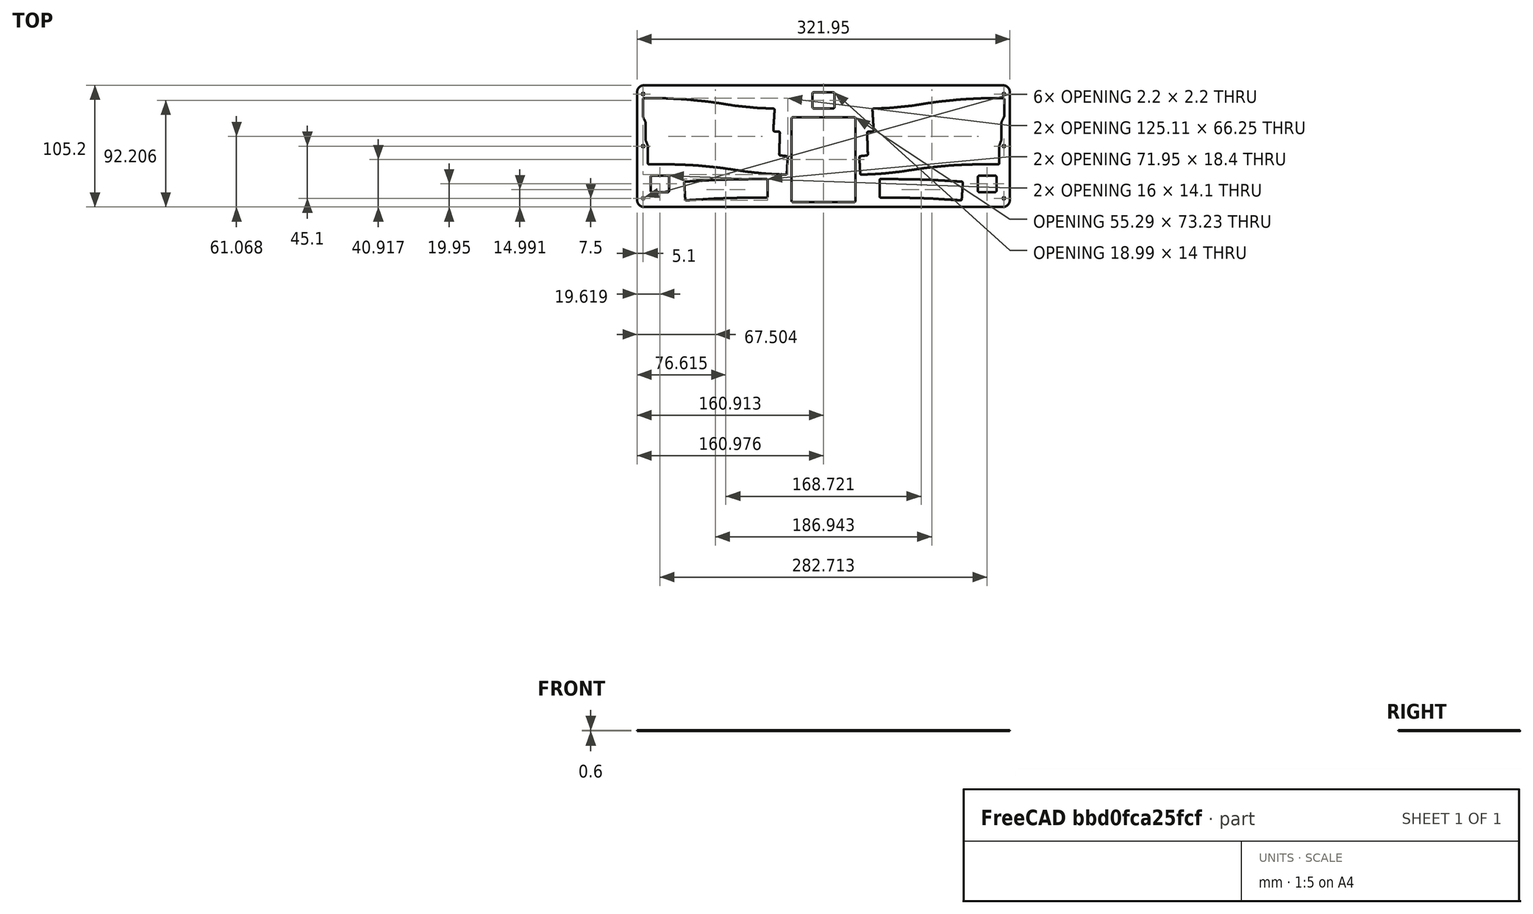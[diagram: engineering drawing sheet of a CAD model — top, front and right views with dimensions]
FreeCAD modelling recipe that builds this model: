
FCSTD DOCUMENT  (FreeCAD 1.0R39109 (Git))
Label: Woorden_decorate
License: All rights reserved
LicenseURL: http://en.wikipedia.org/wiki/All_rights_reserved
objects: Sketcher::SketchObject×1, PartDesign::Pad×1, PartDesign::Body×1
note: 6 computed .brp shape members not serialized (recipe doc carries the construction recipe); baked Part::Feature solids carry a one-line shape summary decoded from their .brp

FEATURE [Sketcher::SketchObject] Sketch
  ArcFitTolerance = 1e-06
  FullyConstrained = false
  MakeInternals = false
  sketch-geometry (177):
    g0: BSplineCurve PolesCount=2 KnotsCount=2 Degree=1 IsPeriodic=0
    g1: BSplineCurve PolesCount=3 KnotsCount=2 Degree=2 IsPeriodic=0
    g2: BSplineCurve PolesCount=3 KnotsCount=2 Degree=2 IsPeriodic=0
    g3: BSplineCurve PolesCount=3 KnotsCount=2 Degree=2 IsPeriodic=0
    g4: BSplineCurve PolesCount=3 KnotsCount=2 Degree=2 IsPeriodic=0
    g5: BSplineCurve PolesCount=3 KnotsCount=2 Degree=2 IsPeriodic=0
    g6: BSplineCurve PolesCount=3 KnotsCount=2 Degree=2 IsPeriodic=0
    g7: BSplineCurve PolesCount=3 KnotsCount=2 Degree=2 IsPeriodic=0
    g8: BSplineCurve PolesCount=3 KnotsCount=2 Degree=2 IsPeriodic=0
    g9: BSplineCurve PolesCount=2 KnotsCount=2 Degree=1 IsPeriodic=0
    g10: BSplineCurve PolesCount=2 KnotsCount=2 Degree=1 IsPeriodic=0
    g11: BSplineCurve PolesCount=2 KnotsCount=2 Degree=1 IsPeriodic=0
    g12: BSplineCurve PolesCount=2 KnotsCount=2 Degree=1 IsPeriodic=0
    g13: BSplineCurve PolesCount=2 KnotsCount=2 Degree=1 IsPeriodic=0
    g14: BSplineCurve PolesCount=2 KnotsCount=2 Degree=1 IsPeriodic=0
    g15: BSplineCurve PolesCount=2 KnotsCount=2 Degree=1 IsPeriodic=0
    g16: BSplineCurve PolesCount=2 KnotsCount=2 Degree=1 IsPeriodic=0
    g17: BSplineCurve PolesCount=3 KnotsCount=2 Degree=2 IsPeriodic=0
    g18: BSplineCurve PolesCount=2 KnotsCount=2 Degree=1 IsPeriodic=0
    g19: BSplineCurve PolesCount=3 KnotsCount=2 Degree=2 IsPeriodic=0
    g20: BSplineCurve PolesCount=3 KnotsCount=2 Degree=2 IsPeriodic=0
    g21: BSplineCurve PolesCount=2 KnotsCount=2 Degree=1 IsPeriodic=0
    g22: BSplineCurve PolesCount=3 KnotsCount=2 Degree=2 IsPeriodic=0
    g23: BSplineCurve PolesCount=2 KnotsCount=2 Degree=1 IsPeriodic=0
    g24: BSplineCurve PolesCount=3 KnotsCount=2 Degree=2 IsPeriodic=0
    g25: BSplineCurve PolesCount=2 KnotsCount=2 Degree=1 IsPeriodic=0
    g26: BSplineCurve PolesCount=2 KnotsCount=2 Degree=1 IsPeriodic=0
    g27: BSplineCurve PolesCount=2 KnotsCount=2 Degree=1 IsPeriodic=0
    g28: BSplineCurve PolesCount=2 KnotsCount=2 Degree=1 IsPeriodic=0
    g29: BSplineCurve PolesCount=3 KnotsCount=2 Degree=2 IsPeriodic=0
    g30: BSplineCurve PolesCount=3 KnotsCount=2 Degree=2 IsPeriodic=0
    g31: BSplineCurve PolesCount=2 KnotsCount=2 Degree=1 IsPeriodic=0
    g32: BSplineCurve PolesCount=2 KnotsCount=2 Degree=1 IsPeriodic=0
    g33: BSplineCurve PolesCount=2 KnotsCount=2 Degree=1 IsPeriodic=0
    g34: BSplineCurve PolesCount=2 KnotsCount=2 Degree=1 IsPeriodic=0
    g35: BSplineCurve PolesCount=3 KnotsCount=2 Degree=2 IsPeriodic=0
    g36: BSplineCurve PolesCount=2 KnotsCount=2 Degree=1 IsPeriodic=0
    g37: BSplineCurve PolesCount=2 KnotsCount=2 Degree=1 IsPeriodic=0
    g38: BSplineCurve PolesCount=3 KnotsCount=2 Degree=2 IsPeriodic=0
    g39: BSplineCurve PolesCount=2 KnotsCount=2 Degree=1 IsPeriodic=0
    g40: BSplineCurve PolesCount=3 KnotsCount=2 Degree=2 IsPeriodic=0
    g41: BSplineCurve PolesCount=2 KnotsCount=2 Degree=1 IsPeriodic=0
    g42: BSplineCurve PolesCount=3 KnotsCount=2 Degree=2 IsPeriodic=0
    g43: BSplineCurve PolesCount=2 KnotsCount=2 Degree=1 IsPeriodic=0
    g44: BSplineCurve PolesCount=2 KnotsCount=2 Degree=1 IsPeriodic=0
    g45: BSplineCurve PolesCount=2 KnotsCount=2 Degree=1 IsPeriodic=0
    g46: BSplineCurve PolesCount=2 KnotsCount=2 Degree=1 IsPeriodic=0
    g47: BSplineCurve PolesCount=2 KnotsCount=2 Degree=1 IsPeriodic=0
    g48: BSplineCurve PolesCount=3 KnotsCount=2 Degree=2 IsPeriodic=0
    g49: BSplineCurve PolesCount=2 KnotsCount=2 Degree=1 IsPeriodic=0
    g50: BSplineCurve PolesCount=3 KnotsCount=2 Degree=2 IsPeriodic=0
    g51: BSplineCurve PolesCount=2 KnotsCount=2 Degree=1 IsPeriodic=0
    g52: BSplineCurve PolesCount=2 KnotsCount=2 Degree=1 IsPeriodic=0
    g53: BSplineCurve PolesCount=2 KnotsCount=2 Degree=1 IsPeriodic=0
    g54: BSplineCurve PolesCount=3 KnotsCount=2 Degree=2 IsPeriodic=0
    g55: BSplineCurve PolesCount=3 KnotsCount=2 Degree=2 IsPeriodic=0
    g56: BSplineCurve PolesCount=2 KnotsCount=2 Degree=1 IsPeriodic=0
    g57: BSplineCurve PolesCount=2 KnotsCount=2 Degree=1 IsPeriodic=0
    g58: BSplineCurve PolesCount=2 KnotsCount=2 Degree=1 IsPeriodic=0
    g59: BSplineCurve PolesCount=2 KnotsCount=2 Degree=1 IsPeriodic=0
    g60: BSplineCurve PolesCount=2 KnotsCount=2 Degree=1 IsPeriodic=0
    g61: BSplineCurve PolesCount=2 KnotsCount=2 Degree=1 IsPeriodic=0
    g62: BSplineCurve PolesCount=2 KnotsCount=2 Degree=1 IsPeriodic=0
    g63: BSplineCurve PolesCount=2 KnotsCount=2 Degree=1 IsPeriodic=0
    g64: BSplineCurve PolesCount=2 KnotsCount=2 Degree=1 IsPeriodic=0
    g65: BSplineCurve PolesCount=2 KnotsCount=2 Degree=1 IsPeriodic=0
    g66: BSplineCurve PolesCount=2 KnotsCount=2 Degree=1 IsPeriodic=0
    g67: BSplineCurve PolesCount=3 KnotsCount=2 Degree=2 IsPeriodic=0
    g68: BSplineCurve PolesCount=2 KnotsCount=2 Degree=1 IsPeriodic=0
    g69: BSplineCurve PolesCount=2 KnotsCount=2 Degree=1 IsPeriodic=0
    g70: BSplineCurve PolesCount=3 KnotsCount=2 Degree=2 IsPeriodic=0
    g71: BSplineCurve PolesCount=3 KnotsCount=2 Degree=2 IsPeriodic=0
    g72: BSplineCurve PolesCount=3 KnotsCount=2 Degree=2 IsPeriodic=0
    g73: BSplineCurve PolesCount=2 KnotsCount=2 Degree=1 IsPeriodic=0
    g74: BSplineCurve PolesCount=3 KnotsCount=2 Degree=2 IsPeriodic=0
    g75: BSplineCurve PolesCount=2 KnotsCount=2 Degree=1 IsPeriodic=0
    g76: BSplineCurve PolesCount=3 KnotsCount=2 Degree=2 IsPeriodic=0
    g77: BSplineCurve PolesCount=2 KnotsCount=2 Degree=1 IsPeriodic=0
    g78: BSplineCurve PolesCount=3 KnotsCount=2 Degree=2 IsPeriodic=0
    g79: BSplineCurve PolesCount=3 KnotsCount=2 Degree=2 IsPeriodic=0
    g80: BSplineCurve PolesCount=3 KnotsCount=2 Degree=2 IsPeriodic=0
    g81: BSplineCurve PolesCount=3 KnotsCount=2 Degree=2 IsPeriodic=0
    g82: BSplineCurve PolesCount=2 KnotsCount=2 Degree=1 IsPeriodic=0
    g83: BSplineCurve PolesCount=3 KnotsCount=2 Degree=2 IsPeriodic=0
    g84: BSplineCurve PolesCount=2 KnotsCount=2 Degree=1 IsPeriodic=0
    g85: BSplineCurve PolesCount=2 KnotsCount=2 Degree=1 IsPeriodic=0
    g86: BSplineCurve PolesCount=2 KnotsCount=2 Degree=1 IsPeriodic=0
    g87: BSplineCurve PolesCount=3 KnotsCount=2 Degree=2 IsPeriodic=0
    g88: BSplineCurve PolesCount=2 KnotsCount=2 Degree=1 IsPeriodic=0
    g89: BSplineCurve PolesCount=3 KnotsCount=2 Degree=2 IsPeriodic=0
    g90: BSplineCurve PolesCount=2 KnotsCount=2 Degree=1 IsPeriodic=0
    g91: BSplineCurve PolesCount=2 KnotsCount=2 Degree=1 IsPeriodic=0
    g92: BSplineCurve PolesCount=2 KnotsCount=2 Degree=1 IsPeriodic=0
    g93: BSplineCurve PolesCount=3 KnotsCount=2 Degree=2 IsPeriodic=0
    g94: BSplineCurve PolesCount=3 KnotsCount=2 Degree=2 IsPeriodic=0
    g95: BSplineCurve PolesCount=2 KnotsCount=2 Degree=1 IsPeriodic=0
    g96: BSplineCurve PolesCount=2 KnotsCount=2 Degree=1 IsPeriodic=0
    g97: BSplineCurve PolesCount=2 KnotsCount=2 Degree=1 IsPeriodic=0
    g98: BSplineCurve PolesCount=2 KnotsCount=2 Degree=1 IsPeriodic=0
    g99: BSplineCurve PolesCount=2 KnotsCount=2 Degree=1 IsPeriodic=0
    g100: BSplineCurve PolesCount=3 KnotsCount=2 Degree=2 IsPeriodic=0
    g101: BSplineCurve PolesCount=3 KnotsCount=2 Degree=2 IsPeriodic=0
    g102: BSplineCurve PolesCount=2 KnotsCount=2 Degree=1 IsPeriodic=0
    g103: BSplineCurve PolesCount=3 KnotsCount=2 Degree=2 IsPeriodic=0
    g104: BSplineCurve PolesCount=2 KnotsCount=2 Degree=1 IsPeriodic=0
    g105: BSplineCurve PolesCount=3 KnotsCount=2 Degree=2 IsPeriodic=0
    g106: BSplineCurve PolesCount=2 KnotsCount=2 Degree=1 IsPeriodic=0
    g107: BSplineCurve PolesCount=3 KnotsCount=2 Degree=2 IsPeriodic=0
    g108: BSplineCurve PolesCount=3 KnotsCount=2 Degree=2 IsPeriodic=0
    g109: BSplineCurve PolesCount=2 KnotsCount=2 Degree=1 IsPeriodic=0
    g110: BSplineCurve PolesCount=2 KnotsCount=2 Degree=1 IsPeriodic=0
    g111: BSplineCurve PolesCount=2 KnotsCount=2 Degree=1 IsPeriodic=0
    g112: BSplineCurve PolesCount=3 KnotsCount=2 Degree=2 IsPeriodic=0
    g113: BSplineCurve PolesCount=2 KnotsCount=2 Degree=1 IsPeriodic=0
    g114: BSplineCurve PolesCount=2 KnotsCount=2 Degree=1 IsPeriodic=0
    g115: BSplineCurve PolesCount=2 KnotsCount=2 Degree=1 IsPeriodic=0
    g116: BSplineCurve PolesCount=2 KnotsCount=2 Degree=1 IsPeriodic=0
    g117: BSplineCurve PolesCount=2 KnotsCount=2 Degree=1 IsPeriodic=0
    g118: BSplineCurve PolesCount=2 KnotsCount=2 Degree=1 IsPeriodic=0
    g119: BSplineCurve PolesCount=3 KnotsCount=2 Degree=2 IsPeriodic=0
    g120: BSplineCurve PolesCount=2 KnotsCount=2 Degree=1 IsPeriodic=0
    g121: BSplineCurve PolesCount=3 KnotsCount=2 Degree=2 IsPeriodic=0
    g122: BSplineCurve PolesCount=2 KnotsCount=2 Degree=1 IsPeriodic=0
    g123: BSplineCurve PolesCount=3 KnotsCount=2 Degree=2 IsPeriodic=0
    g124: BSplineCurve PolesCount=2 KnotsCount=2 Degree=1 IsPeriodic=0
    g125: BSplineCurve PolesCount=2 KnotsCount=2 Degree=1 IsPeriodic=0
    g126: BSplineCurve PolesCount=2 KnotsCount=2 Degree=1 IsPeriodic=0
    g127: BSplineCurve PolesCount=2 KnotsCount=2 Degree=1 IsPeriodic=0
    g128: BSplineCurve PolesCount=3 KnotsCount=2 Degree=2 IsPeriodic=0
    g129: BSplineCurve PolesCount=2 KnotsCount=2 Degree=1 IsPeriodic=0
    g130: BSplineCurve PolesCount=3 KnotsCount=2 Degree=2 IsPeriodic=0
    g131: BSplineCurve PolesCount=3 KnotsCount=2 Degree=2 IsPeriodic=0
    g132: BSplineCurve PolesCount=2 KnotsCount=2 Degree=1 IsPeriodic=0
    g133: BSplineCurve PolesCount=3 KnotsCount=2 Degree=2 IsPeriodic=0
    g134: BSplineCurve PolesCount=3 KnotsCount=2 Degree=2 IsPeriodic=0
    g135: BSplineCurve PolesCount=3 KnotsCount=2 Degree=2 IsPeriodic=0
    g136: BSplineCurve PolesCount=3 KnotsCount=2 Degree=2 IsPeriodic=0
    g137: BSplineCurve PolesCount=2 KnotsCount=2 Degree=1 IsPeriodic=0
    g138: BSplineCurve PolesCount=2 KnotsCount=2 Degree=1 IsPeriodic=0
    g139: BSplineCurve PolesCount=2 KnotsCount=2 Degree=1 IsPeriodic=0
    g140: BSplineCurve PolesCount=2 KnotsCount=2 Degree=1 IsPeriodic=0
    g141: BSplineCurve PolesCount=2 KnotsCount=2 Degree=1 IsPeriodic=0
    g142: BSplineCurve PolesCount=2 KnotsCount=2 Degree=1 IsPeriodic=0
    g143: BSplineCurve PolesCount=3 KnotsCount=2 Degree=2 IsPeriodic=0
    g144: BSplineCurve PolesCount=3 KnotsCount=2 Degree=2 IsPeriodic=0
    g145: BSplineCurve PolesCount=3 KnotsCount=2 Degree=2 IsPeriodic=0
    g146: BSplineCurve PolesCount=2 KnotsCount=2 Degree=1 IsPeriodic=0
    g147: BSplineCurve PolesCount=3 KnotsCount=2 Degree=2 IsPeriodic=0
    g148: BSplineCurve PolesCount=2 KnotsCount=2 Degree=1 IsPeriodic=0
    g149: BSplineCurve PolesCount=3 KnotsCount=2 Degree=2 IsPeriodic=0
    g150: BSplineCurve PolesCount=2 KnotsCount=2 Degree=1 IsPeriodic=0
    g151: BSplineCurve PolesCount=3 KnotsCount=2 Degree=2 IsPeriodic=0
    g152: BSplineCurve PolesCount=2 KnotsCount=2 Degree=1 IsPeriodic=0
    g153: BSplineCurve PolesCount=2 KnotsCount=2 Degree=1 IsPeriodic=0
    g154: BSplineCurve PolesCount=2 KnotsCount=2 Degree=1 IsPeriodic=0
    g155: BSplineCurve PolesCount=3 KnotsCount=2 Degree=2 IsPeriodic=0
    g156: BSplineCurve PolesCount=2 KnotsCount=2 Degree=1 IsPeriodic=0
    g157: BSplineCurve PolesCount=2 KnotsCount=2 Degree=1 IsPeriodic=0
    g158: BSplineCurve PolesCount=2 KnotsCount=2 Degree=1 IsPeriodic=0
    g159: BSplineCurve PolesCount=2 KnotsCount=2 Degree=1 IsPeriodic=0
    g160: BSplineCurve PolesCount=3 KnotsCount=2 Degree=2 IsPeriodic=0
    g161: BSplineCurve PolesCount=3 KnotsCount=2 Degree=2 IsPeriodic=0
    g162: BSplineCurve PolesCount=2 KnotsCount=2 Degree=1 IsPeriodic=0
    g163: BSplineCurve PolesCount=2 KnotsCount=2 Degree=1 IsPeriodic=0
    g164: BSplineCurve PolesCount=2 KnotsCount=2 Degree=1 IsPeriodic=0
    g165: BSplineCurve PolesCount=3 KnotsCount=2 Degree=2 IsPeriodic=0
    g166: BSplineCurve PolesCount=2 KnotsCount=2 Degree=1 IsPeriodic=0
    g167: BSplineCurve PolesCount=2 KnotsCount=2 Degree=1 IsPeriodic=0
    g168: BSplineCurve PolesCount=2 KnotsCount=2 Degree=1 IsPeriodic=0
    g169: BSplineCurve PolesCount=2 KnotsCount=2 Degree=1 IsPeriodic=0
    g170: BSplineCurve PolesCount=2 KnotsCount=2 Degree=1 IsPeriodic=0
    g171: BSplineCurve PolesCount=7 KnotsCount=4 Degree=2 IsPeriodic=0
    g172: BSplineCurve PolesCount=7 KnotsCount=4 Degree=2 IsPeriodic=0
    g173: BSplineCurve PolesCount=7 KnotsCount=4 Degree=2 IsPeriodic=0
    g174: BSplineCurve PolesCount=7 KnotsCount=4 Degree=2 IsPeriodic=0
    g175: BSplineCurve PolesCount=7 KnotsCount=4 Degree=2 IsPeriodic=0
    g176: BSplineCurve PolesCount=7 KnotsCount=4 Degree=2 IsPeriodic=0
  constraints (13):
    c: Coincident(g160,g97)
    c: Coincident(g112,g92)
    c: Coincident(g167,g108)
    c: Coincident(g122,g119)
    c: Coincident(g96,g126)
    c: Coincident(g129,g103)
    c: Coincident(g135,g98)
    c: Coincident(g170,g81)
    c: Coincident(g79,g77)
    c: Coincident(g114,g78)
    c: Coincident(g59,g54)
    c: Coincident(g64,g42)
    c: Coincident(g43,g29)
FEATURE [PartDesign::Pad] Pad
  Direction = (0,0,1)
  Length = 0.6
  Length2 = 10
  Profile = -> Sketch
  ReferenceAxis = -> Sketch [N_Axis]
  Refine = true
  Suppressed = false
  Type = 0
FEATURE [PartDesign::Body] Body
  AllowCompound = false
  Group = -> [Sketch,Pad]
  Origin = -> Origin
  Tip = -> Pad
